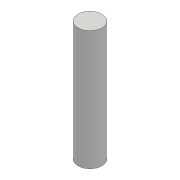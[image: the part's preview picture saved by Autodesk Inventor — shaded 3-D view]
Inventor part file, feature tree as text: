
AUTODESK INVENTOR PART (.ipt)
format: ipt  version: 2017 (Build 210142000, 142)  size: 68,096 bytes
history: native  units: mm
features: extrude x1, sketch x1
ambient origin geometry x8: Origin, YZ Plane, XZ Plane, XY Plane, X Axis, Y Axis, Z Axis, Center Point
bodies: Solid1 (feature_tree)
feature tree (2):
  extrude  "Extrusion1"  Depth=10.0mm TaperAngle=0.0deg
  sketch  "Sketch1"  dims[d0=2.0mm d1=10.0mm d2=0.0mm]
